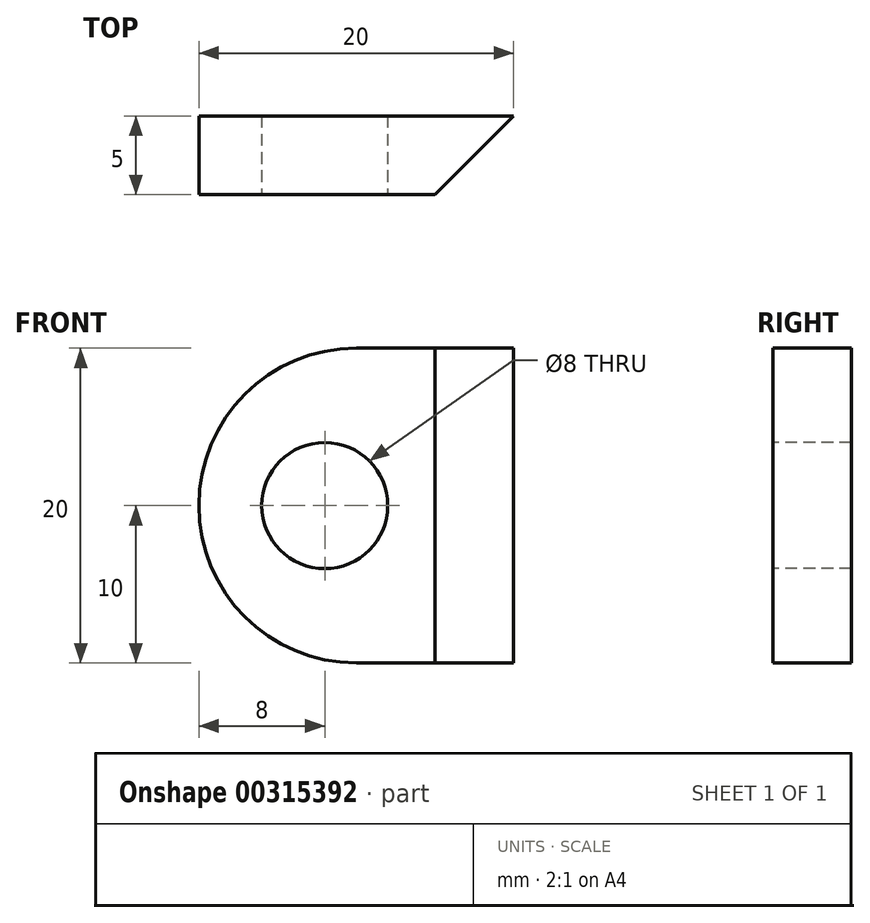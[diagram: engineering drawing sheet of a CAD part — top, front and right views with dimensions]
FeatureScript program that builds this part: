
annotation { "Feature Type Name" : "Feature", "Feature Type Description" : "" }
export const myFeature = defineFeature(function(context is Context, id is Id, definition is map)
    precondition{}
    {
        {
            var Q0;
            Q0=qCreatedBy(makeId("Front.planeOp"),FACE);
            var sketch = newSketch(context, id + "F0", { "sketchPlane" : qUnion([Q0])});
            skLineSegment(sketch, "E0.bottom", {"start": v(-10, 10) * mm, "end": v(10, 10) * mm});
            skLineSegment(sketch, "E0.top", {"start": v(-10, -10) * mm, "end": v(10, -10) * mm});
            skLineSegment(sketch, "E0.left", {"start": v(-10, 10) * mm, "end": v(-10, -10) * mm});
            skLineSegment(sketch, "E0.right", {"start": v(10, 10) * mm, "end": v(10, -10) * mm});
            skPoint(sketch, "E0.middle", {"position": v(0, 0) * mm});
            skSolve(sketch);
        }
        {
            var Q0;
            Q0=makeQuery(id+"F0.imprint","IMPRINT",FACE,{"disambiguationData":[TD([[makeQuery(id+"F0.imprint","IMPRINT",EDGE,{"derivedFrom":sQuery(id+"F0.wireOp",EDGE,"E0.bottom")}),-1.0]])]});
            extrude(context, id + "F1", {"entities" : qUnion([Q0]), "depth" : 5 * mm});
        }
        {
            var Q0;
            Q0=makeQuery(id+"F1.opExtrude","SWEPT_EDGE",EDGE,{"disambiguationData":[OSD([sQuery(id+"F0.wireOp",EDGE,"E0.bottom"),sQuery(id+"F0.wireOp",EDGE,"E0.left")])]});
            var Q1;
            Q1=makeQuery(id+"F1.opExtrude","SWEPT_EDGE",EDGE,{"disambiguationData":[OSD([sQuery(id+"F0.wireOp",EDGE,"E0.top"),sQuery(id+"F0.wireOp",EDGE,"E0.left")])]});
            fillet(context, id + "F2", {"entities" : qUnion([Q0, Q1]), "radius" : 10 * mm, "tangentPropagation" : true, "allowEdgeOverflow" : false});
        }
        {
            var Q0;
            Q0=makeQuery(id+"F1.opExtrude","CAP_FACE",FACE,{"disambiguationData":[OSD([sQuery(id+"F0.wireOp",EDGE,"E0.bottom"),sQuery(id+"F0.wireOp",EDGE,"E0.top"),sQuery(id+"F0.wireOp",EDGE,"E0.left"),sQuery(id+"F0.wireOp",EDGE,"E0.right")])],"isStart":false});
            var sketch = newSketch(context, id + "F3", { "sketchPlane" : qUnion([Q0])});
            skLineSegment(sketch, "E1", {"start": v(-12.5, 0) * mm, "end": v(0, 0) * mm, "construction": true});
            skCircle(sketch, "E2", {"center": v(-2, 0) * mm, "radius": 4 * mm});
            skSolve(sketch);
        }
        {
            var Q0;
            Q0=makeQuery(id+"F3.imprint","IMPRINT",FACE,{"disambiguationData":[TD([[makeQuery(id+"F3.imprint","IMPRINT",EDGE,{"derivedFrom":sQuery(id+"F3.wireOp",EDGE,"E2")}),1.0]])]});
            extrude(context, id + "F4", {"entities" : qUnion([Q0]), "operationType" : NewBodyOperationType.REMOVE, "oppositeDirection" : true, "depth" : 25 * mm});
        }
        {
            var Q0;
            Q0=makeQuery(id+"F1.opExtrude","CAP_EDGE",EDGE,{"disambiguationData":[OSD([sQuery(id+"F0.wireOp",EDGE,"E0.right")])],"isStart":false});
            chamfer(context, id + "F5", {"entities" : qUnion([Q0]), "width" : 5 * mm, "tangentPropagation" : true});
        }
    });
